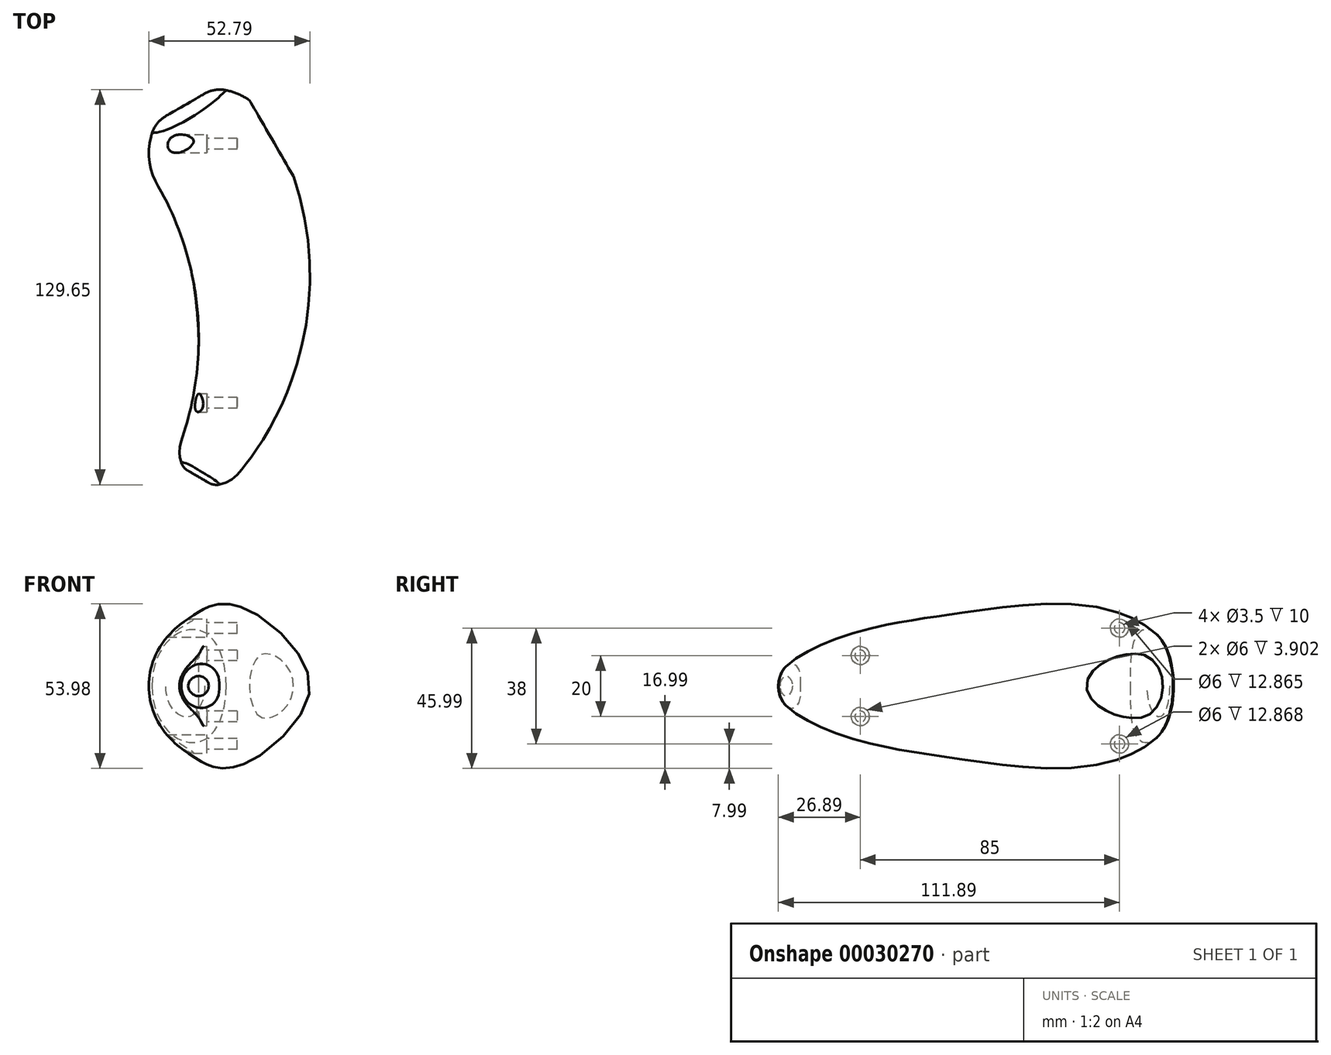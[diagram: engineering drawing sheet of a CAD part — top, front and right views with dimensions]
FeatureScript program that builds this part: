
annotation { "Feature Type Name" : "Feature", "Feature Type Description" : "" }
export const myFeature = defineFeature(function(context is Context, id is Id, definition is map)
    precondition{}
    {
        {
            var Q0;
            Q0=qCreatedBy(makeId("Top.planeOp"),FACE);
            var sketch = newSketch(context, id + "F0", { "sketchPlane" : qUnion([Q0])});
            skLineSegment(sketch, "E0", {"start": v(-73.4, 70) * mm, "end": v(73.4, 70) * mm, "construction": true});
            skLineSegment(sketch, "E1", {"start": v(-73.4, -60) * mm, "end": v(73.4, -60) * mm, "construction": true});
            skPoint(sketch, "E2", {"position": v(0, 70) * mm});
            skPoint(sketch, "E3", {"position": v(0, -60) * mm});
            skArc(sketch, "E4", {"start": v(18.19, 59.5) * mm, "mid": v(-10.5, 67.19) * mm, "end": v(-18.19, 38.5) * mm});
            skArc(sketch, "E5", {"start": v(-10.38, -45.35) * mm, "mid": v(-5.11, -2.57) * mm, "end": v(-18.19, 38.5) * mm});
            skArc(sketch, "E6", {"start": v(-10.38, -45.35) * mm, "mid": v(-5.41, -58.58) * mm, "end": v(8.47, -56.01) * mm});
            skArc(sketch, "E7", {"start": v(8.47, -56.01) * mm, "mid": v(31.43, 0.22) * mm, "end": v(18.19, 59.5) * mm});
            skLineSegment(sketch, "E8", {"start": v(18.19, 59.5) * mm, "end": v(0, 49) * mm, "construction": true});
            skLineSegment(sketch, "E9", {"start": v(0, 70) * mm, "end": v(0, 49) * mm, "construction": true});
            skLineSegment(sketch, "E10", {"start": v(-18.19, 38.5) * mm, "end": v(0, 49) * mm, "construction": true});
            skLineSegment(sketch, "E11", {"start": v(0, 49) * mm, "end": v(0, -49) * mm, "construction": true});
            skPoint(sketch, "E12", {"position": v(0, 0) * mm});
            skLineSegment(sketch, "E13", {"start": v(0, 49) * mm, "end": v(-10.5, 67.19) * mm});
            skLineSegment(sketch, "E14", {"start": v(-10.38, -45.35) * mm, "end": v(0, -49) * mm, "construction": true});
            skLineSegment(sketch, "E15", {"start": v(8.47, -56.01) * mm, "end": v(0, -49) * mm, "construction": true});
            skLineSegment(sketch, "E16", {"start": v(0, -49) * mm, "end": v(-5.41, -58.58) * mm});
            skArc(sketch, "E17", {"start": v(0, -49) * mm, "mid": v(13.13, 0) * mm, "end": v(0, 49) * mm});
            skSolve(sketch);
        }
        {
            var Q0;
            Q0=qCreatedBy(makeId("Right.planeOp"),FACE);
            var sketch = newSketch(context, id + "F1", { "sketchPlane" : qUnion([Q0])});
            skArc(sketch, "E18", {"start": v(68.77, -12.09) * mm, "mid": v(70, 0) * mm, "end": v(68.77, 12.09) * mm});
            skArc(sketch, "E19", {"start": v(68.77, 12.09) * mm, "mid": v(64.24, 20.1) * mm, "end": v(55.88, 23.96) * mm});
            skArc(sketch, "E20", {"start": v(55.88, -23.96) * mm, "mid": v(64.24, -20.1) * mm, "end": v(68.77, -12.09) * mm});
            skArc(sketch, "E21", {"start": v(55.88, 23.96) * mm, "mid": v(0.6, 23.83) * mm, "end": v(-52.99, 10.25) * mm});
            skArc(sketch, "E22", {"start": v(-52.99, -10.25) * mm, "mid": v(0.6, -23.83) * mm, "end": v(55.88, -23.96) * mm});
            skArc(sketch, "E23", {"start": v(-52.99, 10.25) * mm, "mid": v(-60, 0) * mm, "end": v(-52.99, -10.25) * mm});
            skLineSegment(sketch, "E24", {"start": v(54.08, 9.07) * mm, "end": v(0, 0) * mm, "construction": true});
            skLineSegment(sketch, "E25", {"start": v(0, 0) * mm, "end": v(54.08, -9.07) * mm, "construction": true});
            skLineSegment(sketch, "E26", {"start": v(28.77, 199.93) * mm, "end": v(0, 0) * mm, "construction": true});
            skLineSegment(sketch, "E27", {"start": v(28.77, -199.93) * mm, "end": v(0, 0) * mm, "construction": true});
            skPoint(sketch, "E28", {"position": v(-60, 0) * mm});
            skLineSegment(sketch, "E29", {"start": v(-52.99, 10.25) * mm, "end": v(-49, 0) * mm, "construction": true});
            skLineSegment(sketch, "E30", {"start": v(-52.99, -10.25) * mm, "end": v(-49, 0) * mm, "construction": true});
            skSolve(sketch);
        }
        {
            var Q0;
            Q0=qCreatedBy(makeId("Front.planeOp"),FACE);
            var sketch = newSketch(context, id + "F2", { "sketchPlane" : qUnion([Q0])});
            skLineSegment(sketch, "E31", {"start": v(-84.87, -31.26) * mm, "end": v(-84.87, 31.26) * mm, "construction": true});
            skPoint(sketch, "E32", {"position": v(-84.87, 0) * mm});
            skSolve(sketch);
        }
        {
            var Q0;
            Q0=sQuery(id+"F2.wireOp",VERTEX,"E31.end");
            var Q1;
            Q1=sQuery(id+"F2.wireOp",VERTEX,"E31.start");
            var Q2;
            Q2=sQuery(id+"F0.wireOp",VERTEX,"E9.end");
            cPlane(context, id + "F3", {"entities" : qUnion([Q0, Q1, Q2]), "cplaneType" : CPlaneType.THREE_POINT, "offset" : 150 * mm, "width" : 150 * mm, "height" : 150 * mm});
        }
        {
            var Q0;
            Q0=sQuery(id+"F2.wireOp",VERTEX,"E31.end");
            var Q1;
            Q1=sQuery(id+"F2.wireOp",VERTEX,"E31.start");
            var Q2;
            Q2=sQuery(id+"F1.wireOp",VERTEX,"E30.end");
            cPlane(context, id + "F4", {"entities" : qUnion([Q0, Q1, Q2]), "cplaneType" : CPlaneType.THREE_POINT, "offset" : 150 * mm, "width" : 150 * mm, "height" : 150 * mm});
        }
        {
            var Q0;
            Q0=qCreatedBy(id+"F3.planeOp",FACE);
            var Q1;
            Q1=sQuery(id+"F0.wireOp",VERTEX,"E2");
            cPlane(context, id + "F5", {"entities" : qUnion([Q0, Q1]), "cplaneType" : CPlaneType.PLANE_POINT, "offset" : 150 * mm, "width" : 150 * mm, "height" : 150 * mm});
        }
        {
            var Q0;
            Q0=qCreatedBy(id+"F4.planeOp",FACE);
            var Q1;
            Q1=sQuery(id+"F1.wireOp",VERTEX,"E28");
            cPlane(context, id + "F6", {"entities" : qUnion([Q0, Q1]), "cplaneType" : CPlaneType.PLANE_POINT, "offset" : 150 * mm, "width" : 150 * mm, "height" : 150 * mm});
        }
        {
            var Q0;
            Q0=qCreatedBy(id+"F5.planeOp",FACE);
            var sketch = newSketch(context, id + "F7", { "sketchPlane" : qUnion([Q0])});
            skPoint(sketch, "E33", {"position": v(-14, 0) * mm});
            skEllipse(sketch, "E34", {"center": v(-24.5, 0) * mm, "majorRadius": 15 * mm, "minorRadius": 10.5 * mm, "majorAxis": v(0, 1)});
            skPoint(sketch, "E35", {"position": v(-35, 0) * mm});
            skPoint(sketch, "E36", {"position": v(-24.5, 15) * mm});
            skPoint(sketch, "E37", {"position": v(-24.5, -15) * mm});
            skSolve(sketch);
        }
        {
            var Q0;
            Q0=qCreatedBy(id+"F3.planeOp",FACE);
            var sketch = newSketch(context, id + "F8", { "sketchPlane" : qUnion([Q0])});
            skEllipse(sketch, "E38", {"center": v(-24.5, 0) * mm, "majorRadius": 21 * mm, "minorRadius": 24.68 * mm, "majorAxis": v(1, 0)});
            skPoint(sketch, "E39", {"position": v(-24.5, 24.68) * mm});
            skPoint(sketch, "E40", {"position": v(-24.5, -24.68) * mm});
            skSolve(sketch);
        }
        {
            var Q0;
            Q0=qCreatedBy(makeId("Front.planeOp"),FACE);
            var sketch = newSketch(context, id + "F9", { "sketchPlane" : qUnion([Q0])});
            skPoint(sketch, "E41", {"position": v(0, -23.75) * mm});
            skPoint(sketch, "E42", {"position": v(-5.38, 0) * mm});
            skPoint(sketch, "E43", {"position": v(0, 23.75) * mm});
            skPoint(sketch, "E44", {"position": v(31.41, 0) * mm});
            skFitSpline(sketch, "E45", {"points": [v(-5.38, 0) * mm, v(0, 23.75) * mm, v(31.41, 0) * mm, v(0, -23.75) * mm, v(-5.38, 0) * mm]});
            skSolve(sketch);
        }
        {
            var Q0;
            Q0=qCreatedBy(id+"F4.planeOp",FACE);
            var sketch = newSketch(context, id + "F10", { "sketchPlane" : qUnion([Q0])});
            skPoint(sketch, "E46", {"position": v(-35.64, 0) * mm});
            skPoint(sketch, "E47", {"position": v(-24.5, 11.76) * mm});
            skPoint(sketch, "E48", {"position": v(-13.29, 0) * mm});
            skPoint(sketch, "E49", {"position": v(-24.5, -11.76) * mm});
            skFitSpline(sketch, "E50", {"points": [v(-13.29, 0) * mm, v(-24.5, -11.76) * mm, v(-35.64, 0) * mm, v(-24.5, 11.76) * mm, v(-13.29, 0) * mm]});
            skSolve(sketch);
        }
        {
            var Q0;
            Q0=qCreatedBy(id+"F6.planeOp",FACE);
            var sketch = newSketch(context, id + "F11", { "sketchPlane" : qUnion([Q0])});
            skCircle(sketch, "E51", {"center": v(-24.5, 0) * mm, "radius": 5.5 * mm});
            skPoint(sketch, "E52", {"position": v(-19, 0) * mm});
            skSolve(sketch);
        }
        {
            var Q0;
            Q0=qCreatedBy(makeId("Top.planeOp"),FACE);
            var sketch = newSketch(context, id + "F12", { "sketchPlane" : qUnion([Q0])});
            skArc(sketch, "E53.0", {"start": v(-18.19, 59.5) * mm, "mid": v(-21, 49) * mm, "end": v(-18.19, 38.5) * mm});
            skArc(sketch, "E53.1", {"start": v(-10.38, -45.35) * mm, "mid": v(-5.11, -2.57) * mm, "end": v(-18.19, 38.5) * mm});
            skArc(sketch, "E53.2", {"start": v(-10.38, -45.35) * mm, "mid": v(-10.95, -50.02) * mm, "end": v(-9.53, -54.5) * mm});
            skPoint(sketch, "E54", {"position": v(-18.19, 59.5) * mm});
            skPoint(sketch, "E55.orphan", {"position": v(18.19, 59.5) * mm});
            skPoint(sketch, "E56", {"position": v(-9.53, -54.5) * mm});
            skPoint(sketch, "E57.orphan", {"position": v(8.47, -56.01) * mm});
            skSolve(sketch);
        }
        {
            var Q0;
            Q0=qCreatedBy(makeId("Top.planeOp"),FACE);
            var sketch = newSketch(context, id + "F13", { "sketchPlane" : qUnion([Q0])});
            skArc(sketch, "E58.0", {"start": v(18.19, 59.5) * mm, "mid": v(10.5, 67.19) * mm, "end": v(0, 70) * mm});
            skArc(sketch, "E58.1", {"start": v(8.47, -56.01) * mm, "mid": v(31.43, 0.22) * mm, "end": v(18.19, 59.5) * mm});
            skArc(sketch, "E58.2", {"start": v(0, -60) * mm, "mid": v(4.68, -58.95) * mm, "end": v(8.47, -56.01) * mm});
            skPoint(sketch, "E59", {"position": v(0, 70) * mm});
            skPoint(sketch, "E60", {"position": v(0, -60) * mm});
            skPoint(sketch, "E61.orphan", {"position": v(-18.19, 38.5) * mm});
            skPoint(sketch, "E62.orphan", {"position": v(-10.38, -45.35) * mm});
            skSolve(sketch);
        }
        {
            var Q0;
            Q0=makeQuery(id+"F7.imprint","IMPRINT",FACE,{"disambiguationData":[TD([[makeQuery(id+"F7.imprint","IMPRINT",EDGE,{"derivedFrom":sQuery(id+"F7.wireOp",EDGE,"E34")}),1.0]])]});
            var Q1;
            Q1=makeQuery(id+"F8.imprint","IMPRINT",FACE,{"disambiguationData":[TD([[makeQuery(id+"F8.imprint","IMPRINT",EDGE,{"derivedFrom":sQuery(id+"F8.wireOp",EDGE,"E38")}),1.0]])]});
            var Q2;
            Q2=makeQuery(id+"F9.imprint","IMPRINT",FACE,{"disambiguationData":[TD([[makeQuery(id+"F9.imprint","IMPRINT",EDGE,{"derivedFrom":sQuery(id+"F9.wireOp",EDGE,"E45")}),-1.0]])]});
            var Q3;
            Q3=makeQuery(id+"F10.imprint","IMPRINT",FACE,{"disambiguationData":[TD([[makeQuery(id+"F10.imprint","IMPRINT",EDGE,{"derivedFrom":sQuery(id+"F10.wireOp",EDGE,"E50")}),-1.0]])]});
            var Q4;
            Q4 = qSketchRegion(id + "F11", true);
            var Q5;
            Q5 = qConstructionFilter(qBodyType(qCreatedBy(id + "F12" ,EDGE), BodyType.WIRE), ConstructionObject.NO);
            var Q6;
            Q6 = qConstructionFilter(qBodyType(qCreatedBy(id + "F13" ,EDGE), BodyType.WIRE), ConstructionObject.NO);
            loft(context, id + "F14", {"addGuides" : true, "sheetProfilesArray" : [{ "sheetProfileEntities" : qUnion([Q0]) }, { "sheetProfileEntities" : qUnion([Q1]) }, { "sheetProfileEntities" : qUnion([Q2]) }, { "sheetProfileEntities" : qUnion([Q3]) }, { "sheetProfileEntities" : qUnion([Q4]) }], "guidesArray" : [{ "guideEntities" : qUnion([Q5]), "guideDerivativeType" : LoftGuideDerivativeType.DEFAULT, "guideDerivativeMagnitude" : 1 }, { "guideEntities" : qUnion([Q6]), "guideDerivativeType" : LoftGuideDerivativeType.DEFAULT, "guideDerivativeMagnitude" : 1 }]});
        }
        {
            var Q0;
            Q0=makeQuery(id+"F14.opLoft","MID_CAP_EDGE",EDGE,{"disambiguationData":[OSD([sQuery(id+"F7.wireOp",EDGE,"E34"),sQuery(id+"F12.wireOp",EDGE,"E53.0"),sQuery(id+"F13.wireOp",EDGE,"E58.0")]),OD(0.0)],"capPos":0.0});
            fillet(context, id + "F15", {"entities" : qUnion([Q0]), "radius" : 10 * mm, "tangentPropagation" : true, "allowEdgeOverflow" : false});
        }
        {
            var Q0;
            Q0=makeQuery(id+"F14.opLoft","CAP_FACE",FACE,{"disambiguationData":[OSD([makeQuery(id+"F11.imprint","IMPRINT",FACE,{"disambiguationData":[TD([[makeQuery(id+"F11.imprint","IMPRINT",EDGE,{"derivedFrom":sQuery(id+"F11.wireOp",EDGE,"E51")}),1.0]])]})])],"isStart":true});
            fillet(context, id + "F16", {"entities" : qUnion([Q0]), "radius" : 5 * mm, "tangentPropagation" : true, "allowEdgeOverflow" : false});
        }
        {
            var Q0;
            Q0=qCreatedBy(id+"F3.planeOp",FACE);
            var sketch = newSketch(context, id + "F17", { "sketchPlane" : qUnion([Q0])});
            skLineSegment(sketch, "E63", {"start": v(-24.5, 24.68) * mm, "end": v(-24.5, -24.68) * mm});
            skSolve(sketch);
        }
        {
            var Q0;
            Q0=sQuery(id+"F17.wireOp",VERTEX,"E63.end");
            var Q1;
            Q1=sQuery(id+"F17.wireOp",VERTEX,"E63.start");
            var Q2;
            Q2=sQuery(id+"F0.wireOp",VERTEX,"E13.end");
            cPlane(context, id + "F18", {"entities" : qUnion([Q0, Q1, Q2]), "cplaneType" : CPlaneType.THREE_POINT, "offset" : 150 * mm, "width" : 150 * mm, "height" : 150 * mm});
        }
        {
            var Q0;
            Q0=qCreatedBy(id+"F18.planeOp",FACE);
            cPlane(context, id + "F19", {"entities" : qUnion([Q0]), "cplaneType" : CPlaneType.OFFSET, "offset" : 25 * mm, "width" : 150 * mm, "height" : 150 * mm});
        }
        {
            var Q0;
            Q0=qCreatedBy(id+"F19.planeOp",FACE);
            var sketch = newSketch(context, id + "F20", { "sketchPlane" : qUnion([Q0])});
            skCircle(sketch, "E64", {"center": v(42.44, 0) * mm, "radius": 21.05 * mm});
            skSolve(sketch);
        }
        {
            var Q0;
            Q0=makeQuery(id+"F20.imprint","IMPRINT",FACE,{"disambiguationData":[TD([[makeQuery(id+"F20.imprint","IMPRINT",EDGE,{"derivedFrom":sQuery(id+"F20.wireOp",EDGE,"E64")}),1.0]])]});
            extrude(context, id + "F21", {"entities" : qUnion([Q0]), "operationType" : NewBodyOperationType.REMOVE, "oppositeDirection" : true, "depth" : 6 * mm});
        }
        {
            var Q0;
            Q0=qCreatedBy(makeId("Right.planeOp"),FACE);
            var sketch = newSketch(context, id + "F22", { "sketchPlane" : qUnion([Q0])});
            skLineSegment(sketch, "E65", {"start": v(52, 19) * mm, "end": v(52, -19) * mm, "construction": true});
            skLineSegment(sketch, "E66", {"start": v(-33, 10) * mm, "end": v(-33, -10) * mm, "construction": true});
            skPoint(sketch, "E67", {"position": v(52, 0) * mm});
            skPoint(sketch, "E68", {"position": v(-33, 0) * mm});
            skCircle(sketch, "E69", {"center": v(52, 19) * mm, "radius": 3 * mm});
            skCircle(sketch, "E70", {"center": v(52, -19) * mm, "radius": 3 * mm});
            skCircle(sketch, "E71", {"center": v(-33, 10) * mm, "radius": 3 * mm});
            skCircle(sketch, "E72", {"center": v(-33, -10) * mm, "radius": 3 * mm});
            skSolve(sketch);
        }
        {
            var Q0;
            Q0 = qSketchRegion(id + "F22", true);
            extrude(context, id + "F23", {"entities" : qUnion([Q0]), "operationType" : NewBodyOperationType.REMOVE, "endBound" : BoundingType.THROUGH_ALL, "oppositeDirection" : true, "depth" : 25 * mm});
        }
        {
            var Q0;
            Q0=makeQuery(id+"F1.imprint","IMPRINT",FACE,{"disambiguationData":[TD([[makeQuery(id+"F1.imprint","IMPRINT",EDGE,{"derivedFrom":sQuery(id+"F1.wireOp",EDGE,"E18")}),1.0]])]});
            var sketch = newSketch(context, id + "F24", { "sketchPlane" : qUnion([Q0])});
            skCircle(sketch, "E73", {"center": v(52, 19) * mm, "radius": 1.75 * mm});
            skCircle(sketch, "E74", {"center": v(52, -19) * mm, "radius": 1.75 * mm});
            skSolve(sketch);
        }
        {
            var Q0;
            Q0 = qSketchRegion(id + "F24", true);
            extrude(context, id + "F25", {"entities" : qUnion([Q0]), "operationType" : NewBodyOperationType.REMOVE, "depth" : 8 * mm});
        }
        {
            var Q0;
            Q0=qCreatedBy(makeId("Right.planeOp"),FACE);
            var sketch = newSketch(context, id + "F26", { "sketchPlane" : qUnion([Q0])});
            skCircle(sketch, "E75.0", {"center": v(-33, -10) * mm, "radius": 3 * mm});
            skCircle(sketch, "E75.1", {"center": v(-33, 10) * mm, "radius": 3 * mm});
            skSolve(sketch);
        }
        {
            var Q0;
            Q0=makeQuery(id+"F26.imprint","IMPRINT",FACE,{"disambiguationData":[TD([[makeQuery(id+"F26.imprint","IMPRINT",EDGE,{"derivedFrom":sQuery(id+"F26.wireOp",EDGE,"E75.1")}),1.0]])]});
            var Q1;
            Q1=makeQuery(id+"F26.imprint","IMPRINT",FACE,{"disambiguationData":[TD([[makeQuery(id+"F26.imprint","IMPRINT",EDGE,{"derivedFrom":sQuery(id+"F26.wireOp",EDGE,"E75.0")}),1.0]])]});
            extrude(context, id + "F27", {"entities" : qUnion([Q0, Q1]), "operationType" : NewBodyOperationType.ADD, "oppositeDirection" : true, "depth" : 2 * mm});
        }
        {
            var Q0;
            Q0=makeQuery(id+"F1.imprint","IMPRINT",FACE,{"disambiguationData":[TD([[makeQuery(id+"F1.imprint","IMPRINT",EDGE,{"derivedFrom":sQuery(id+"F1.wireOp",EDGE,"E18")}),1.0]])]});
            var sketch = newSketch(context, id + "F28", { "sketchPlane" : qUnion([Q0])});
            skCircle(sketch, "E76.0", {"center": v(52, -19) * mm, "radius": 3 * mm});
            skCircle(sketch, "E77.0", {"center": v(52, -19) * mm, "radius": 1.75 * mm});
            skCircle(sketch, "E78.0", {"center": v(52, 19) * mm, "radius": 3 * mm});
            skCircle(sketch, "E79.0", {"center": v(52, 19) * mm, "radius": 1.75 * mm});
            skSolve(sketch);
        }
        {
            var Q0;
            Q0 = qSketchRegion(id + "F28", true);
            extrude(context, id + "F29", {"entities" : qUnion([Q0]), "operationType" : NewBodyOperationType.ADD, "oppositeDirection" : true, "depth" : 2 * mm});
        }
        {
            var Q0;
            Q0=makeQuery(id+"F27.opExtrude","CAP_FACE",FACE,{"disambiguationData":[OSD([sQuery(id+"F26.wireOp",EDGE,"E75.1")])],"isStart":false});
            var sketch = newSketch(context, id + "F30", { "sketchPlane" : qUnion([Q0])});
            skCircle(sketch, "E80", {"center": v(33, 10) * mm, "radius": 1.75 * mm});
            skCircle(sketch, "E81", {"center": v(33, -10) * mm, "radius": 1.75 * mm});
            skSolve(sketch);
        }
        {
            var Q0;
            Q0 = qSketchRegion(id + "F30", true);
            extrude(context, id + "F31", {"entities" : qUnion([Q0]), "operationType" : NewBodyOperationType.REMOVE, "oppositeDirection" : true, "depth" : 10 * mm});
        }
    });
